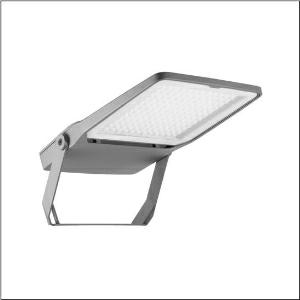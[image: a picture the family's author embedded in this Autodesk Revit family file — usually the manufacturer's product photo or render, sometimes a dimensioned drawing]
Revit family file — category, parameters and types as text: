
# Revit family: floodlight_fl_20_midi___pl52_5xa7682e2d1ac_b47e
name_source: partatom
category: Lighting Fixtures
units: mm (PartAtom-declared; Revit-internal decimal feet)

## family parameters
Cut with Voids When Loaded = No
Host = Face
Light Source = No
Part Type = Normal
Room Calculation Point = No
Round Connector Dimension = Use Diameter
Shared = No

## types (1)
- --- (1 x LED 4000K / CRI = 70 (unbekannt), 26840 lm, 4000K)
    Apparent Load = 208 VA
    CIE Flux Codes = 27 59 98 100 100
    Color Rendering = 70
    Color Temperature = 4000K
    Default Elevation = 1800 mm
    Description = Floodlight FL 20 midi, floodlight, primary light control with lens, of plastic, primary optical cover: protective disc, of toughened safety glass, transparent, light distribution: PL52, light emission: direct distribution, primary light characteristic: asymmetric, installation type: surface-mounted, LED, High Power LED, rated luminous flux: 26.840lm, luminous efficacy: 129lm/W, light colour: 740, colour temperature: 4000K, control gear: ECG Plus, control: flexible luminous flux parameterisation, time-dependent luminous flux control, digital communication interface, power reduction, overheat protection, electronic power reduction, with terminal, 5-pole, max. 2.5mm², mains connection: 220..240V, AC, 50/60Hz, rated input power: 208W, LED unit, of diecast aluminium, powder-coated, Siteco® metallic grey (DB 702S), corrosivity category C5 mid according to DIN EN ISO 12944, incl. 1x M20 cable gland for cable Ø 6.5..12mm, length: 654mm, width: 450mm, height: 76mm, housing frame, of diecast aluminium, powder-coated, Siteco® metallic grey (DB 702S), mounting bracket, of steel, powder-coated, Siteco® metallic grey (DB 702S), DALI, protection rating (complete): IP66, insulation class (complete): insulation class II (safety insulation), certification: CE, ENEC, VDE, protection symbol: D, permissible operating ambient temperature: -40..+40°C, permissible operating ambient temperature for outdoor applications: -40..+50°C, standard: DIN EN 12944, packaging unit: 1 piece

Light Distribution: PL52
    Height = 76 mm
    Lamp = 1 x LED 4000K / CRI >= 70 (unbekannt)
    Lamp Light Flux = 26840 lm
    Lamp count = 1
    Length = 672 mm
    Luminous efficacy = 129 lm/W
    Manufacturer = Siteco
    ModVariant = No
    Model = 5XA7682E2D1AC
    Mounting Place = Wall
    Mounting Type = Surface mounted
    Number of Poles = 1
    OnlyDefault = Yes
    Power Factor = 1
    Product Name = Floodlight FL 20 midi | PL52
    Product group = floodlight | wall mounted
    ProductGroupID = 2001
    Protection Class = Protection class II
    Protection Degree = IP 66
    RLX_Detail_Level = 1
    RLX_Emergency_Light_Flux = 0 lm
    RLX_Emergency_Type = 0
    RLX_Emergency_Type_DB = No
    RlxData = <blob elided: 97973 chars, md5=cc7f0aae>
    Socket = socket
    Standby Power = 0 W
    System Light Flux = 26840 lm
    System Power = 208 W
    Type Comments = factory setting: luminous flux: 100 % | dim-lin: 254 | 484 mA
    Type Image = l_1005943.jpg
    URL = http://relux.com
    VarID = @adj_147605
    Voltage = 0 V
    Weight = 0.00 kg
    Width = 450 mm

## geometry (parser evidence)
native form markers: Blend x4, Sweep x10
no freeform markers — native parametric forms only
